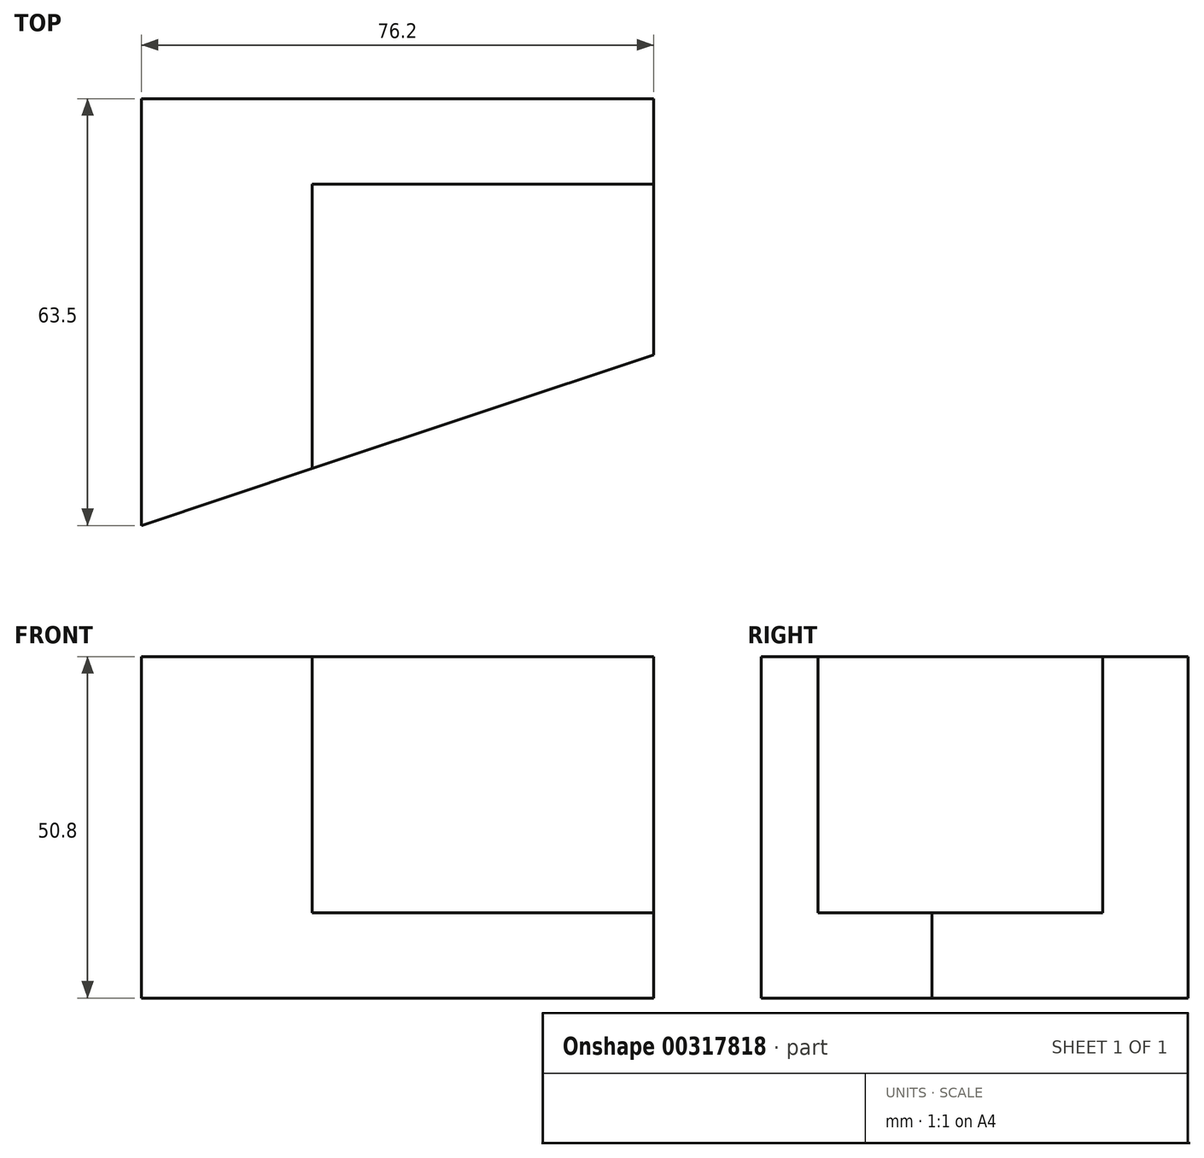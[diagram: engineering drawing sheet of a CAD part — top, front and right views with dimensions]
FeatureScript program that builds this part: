
annotation { "Feature Type Name" : "Feature", "Feature Type Description" : "" }
export const myFeature = defineFeature(function(context is Context, id is Id, definition is map)
    precondition{}
    {
        {
            var Q0;
            Q0=qCreatedBy(makeId("Front.planeOp"),FACE);
            var sketch = newSketch(context, id + "F0", { "sketchPlane" : qUnion([Q0])});
            skLineSegment(sketch, "E0", {"start": v(0, 0) * mm, "end": v(0, 50.8) * mm});
            skLineSegment(sketch, "E1", {"start": v(0, 50.8) * mm, "end": v(76.2, 50.8) * mm});
            skLineSegment(sketch, "E2", {"start": v(0, 0) * mm, "end": v(76.2, 0) * mm});
            skLineSegment(sketch, "E3", {"start": v(76.2, 0) * mm, "end": v(76.2, 50.8) * mm});
            skSolve(sketch);
        }
        {
            var Q0;
            Q0 = qSketchRegion(id + "F0", true);
            extrude(context, id + "F1", {"entities" : qUnion([Q0]), "depth" : 63.5 * mm});
        }
        {
            var Q0;
            Q0=makeQuery(id+"F1.opExtrude","CAP_FACE",FACE,{"disambiguationData":[OSD([sQuery(id+"F0.wireOp",EDGE,"E0"),sQuery(id+"F0.wireOp",EDGE,"E1"),sQuery(id+"F0.wireOp",EDGE,"E2"),sQuery(id+"F0.wireOp",EDGE,"E3")])],"isStart":false});
            var sketch = newSketch(context, id + "F2", { "sketchPlane" : qUnion([Q0])});
            skLineSegment(sketch, "E4", {"start": v(25.4, 50.8) * mm, "end": v(25.4, 12.7) * mm});
            skLineSegment(sketch, "E5", {"start": v(25.4, 12.7) * mm, "end": v(76.2, 12.7) * mm});
            skLineSegment(sketch, "E6", {"start": v(25.4, 50.8) * mm, "end": v(76.2, 50.8) * mm});
            skLineSegment(sketch, "E7", {"start": v(76.2, 50.8) * mm, "end": v(76.2, 12.7) * mm});
            skSolve(sketch);
        }
        {
            var Q0;
            Q0 = qSketchRegion(id + "F2", true);
            extrude(context, id + "F3", {"entities" : qUnion([Q0]), "operationType" : NewBodyOperationType.REMOVE, "oppositeDirection" : true, "depth" : 50.8 * mm});
        }
        {
            var Q0;
            Q0=makeQuery(id+"F1.opExtrude","SWEPT_FACE",FACE,{"disambiguationData":[OSD([sQuery(id+"F0.wireOp",EDGE,"E2")])]});
            var sketch = newSketch(context, id + "F4", { "sketchPlane" : qUnion([Q0])});
            skLineSegment(sketch, "E8", {"start": v(0, 63.5) * mm, "end": v(76.2, 38.1) * mm});
            skLineSegment(sketch, "E9", {"start": v(76.2, 38.1) * mm, "end": v(76.2, 63.5) * mm});
            skLineSegment(sketch, "E10", {"start": v(76.2, 63.5) * mm, "end": v(0, 63.5) * mm});
            skSolve(sketch);
        }
        {
            var Q0;
            Q0 = qSketchRegion(id + "F4", true);
            extrude(context, id + "F5", {"entities" : qUnion([Q0]), "operationType" : NewBodyOperationType.REMOVE, "endBound" : BoundingType.THROUGH_ALL, "oppositeDirection" : true, "depth" : 25.4 * mm});
        }
    });
